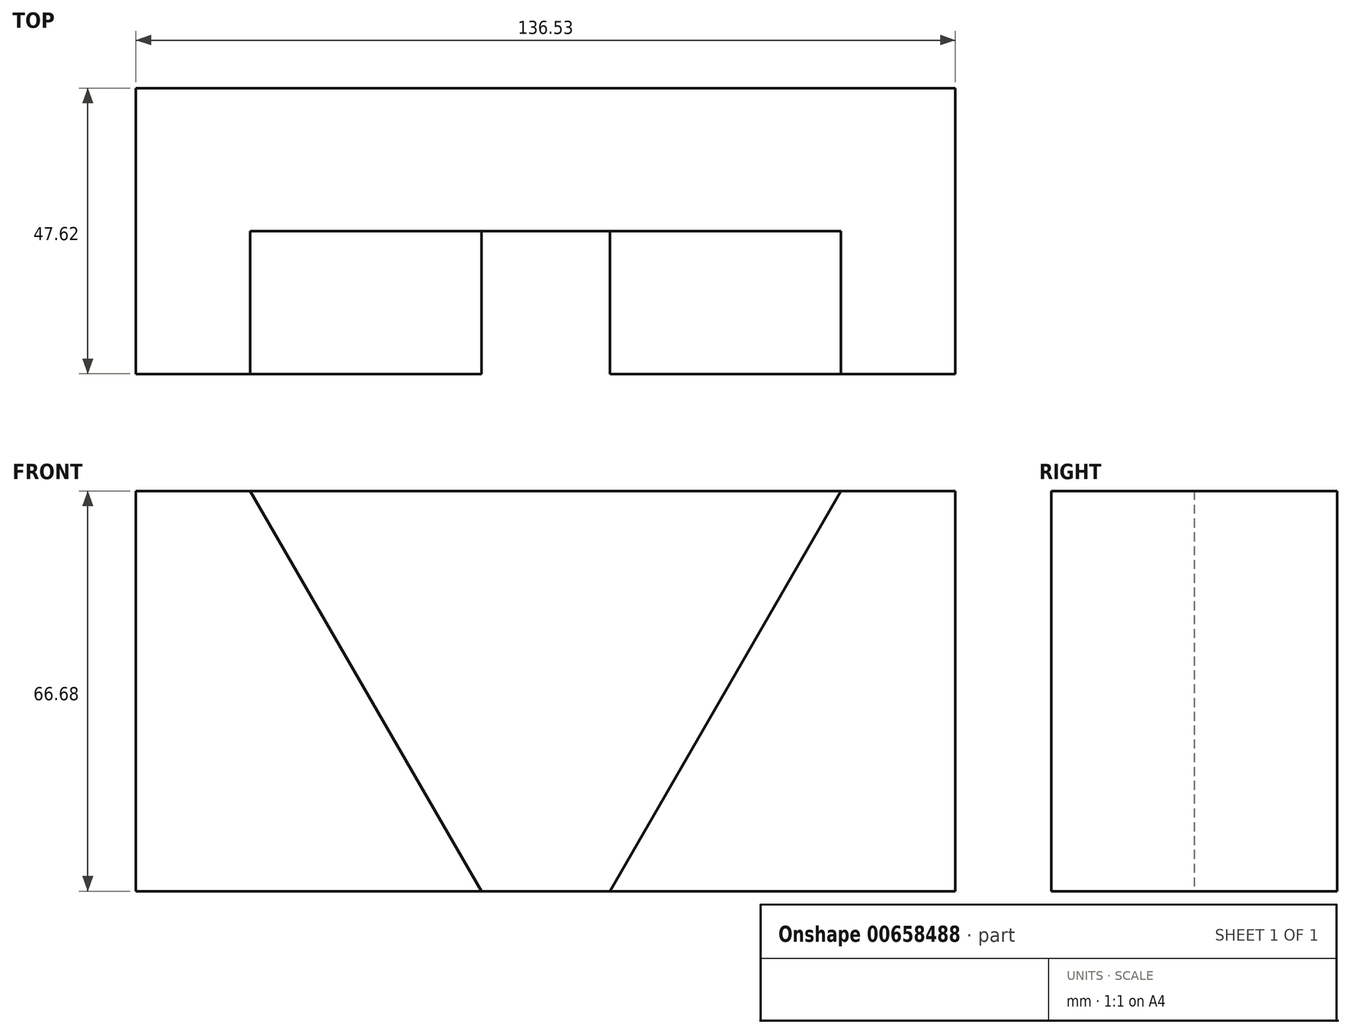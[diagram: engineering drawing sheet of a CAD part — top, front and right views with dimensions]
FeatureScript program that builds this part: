
annotation { "Feature Type Name" : "Feature", "Feature Type Description" : "" }
export const myFeature = defineFeature(function(context is Context, id is Id, definition is map)
    precondition{}
    {
        {
            var Q0;
            Q0=qCreatedBy(makeId("Front.planeOp"),FACE);
            var sketch = newSketch(context, id + "F0", { "sketchPlane" : qUnion([Q0])});
            skLineSegment(sketch, "E0", {"start": v(-74.06, 0) * mm, "end": v(-74.06, 66.68) * mm});
            skLineSegment(sketch, "E1", {"start": v(-74.06, 66.68) * mm, "end": v(62.47, 66.68) * mm});
            skLineSegment(sketch, "E2", {"start": v(62.47, 66.68) * mm, "end": v(62.47, 0) * mm});
            skLineSegment(sketch, "E3", {"start": v(-74.06, 0) * mm, "end": v(62.47, 0) * mm});
            skSolve(sketch);
        }
        {
            var Q0;
            Q0=makeQuery(id+"F0.imprint","IMPRINT",FACE,{"disambiguationData":[TD([[makeQuery(id+"F0.imprint","IMPRINT",EDGE,{"derivedFrom":sQuery(id+"F0.wireOp",EDGE,"E0")}),-1.0]])]});
            extrude(context, id + "F1", {"entities" : qUnion([Q0]), "depth" : 47.62 * mm, "offsetDistance" : 25.4 * mm});
        }
        {
            var Q0;
            Q0=makeQuery(id+"F1.opExtrude","CAP_FACE",FACE,{"disambiguationData":[OSD([sQuery(id+"F0.wireOp",EDGE,"E0"),sQuery(id+"F0.wireOp",EDGE,"E1"),sQuery(id+"F0.wireOp",EDGE,"E2"),sQuery(id+"F0.wireOp",EDGE,"E3")])],"isStart":false});
            var sketch = newSketch(context, id + "F2", { "sketchPlane" : qUnion([Q0])});
            skLineSegment(sketch, "E4", {"start": v(62.47, 66.68) * mm, "end": v(43.42, 66.68) * mm, "construction": true});
            skLineSegment(sketch, "E5", {"start": v(-74.06, 66.68) * mm, "end": v(-55, 66.68) * mm, "construction": true});
            skLineSegment(sketch, "E6", {"start": v(-55, 66.68) * mm, "end": v(-16.51, 0) * mm});
            skLineSegment(sketch, "E7", {"start": v(43.42, 66.68) * mm, "end": v(4.93, 0) * mm});
            skLineSegment(sketch, "E8", {"start": v(-55, 66.68) * mm, "end": v(43.42, 66.68) * mm});
            skLineSegment(sketch, "E9", {"start": v(-16.51, 0) * mm, "end": v(4.93, 0) * mm});
            skSolve(sketch);
        }
        {
            var Q0;
            Q0=makeQuery(id+"F2.imprint","IMPRINT",FACE,{"disambiguationData":[TD([[makeQuery(id+"F2.imprint","IMPRINT",EDGE,{"derivedFrom":sQuery(id+"F2.wireOp",EDGE,"E6")}),1.0]])]});
            extrude(context, id + "F3", {"entities" : qUnion([Q0]), "operationType" : NewBodyOperationType.REMOVE, "oppositeDirection" : true, "depth" : 23.8 * mm, "offsetDistance" : 25.4 * mm});
        }
    });
